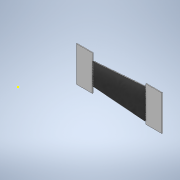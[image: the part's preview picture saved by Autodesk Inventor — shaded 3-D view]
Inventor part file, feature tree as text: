
AUTODESK INVENTOR PART (.ipt)
format: ipt  version: 2020 (Build 240168000, 168)  size: 413,696 bytes
history: native  units: in
note: dims shown in document units (in); Inventor stores cm internally (conversion verified against a paired STEP export)
features: sketch x1, extrude x1
ambient origin geometry x8: Origin, YZ Plane, XZ Plane, XY Plane, X Axis, Y Axis, Z Axis, Center Point
bodies: Solid1 (feature_tree)
feature tree (2):
  sketch  "Sketch1"  dims[d0=0.005in d1=0.0in d2=0.5in d3=0.0344in]
  extrude  "Extrusion1"  Depth=0.005in
